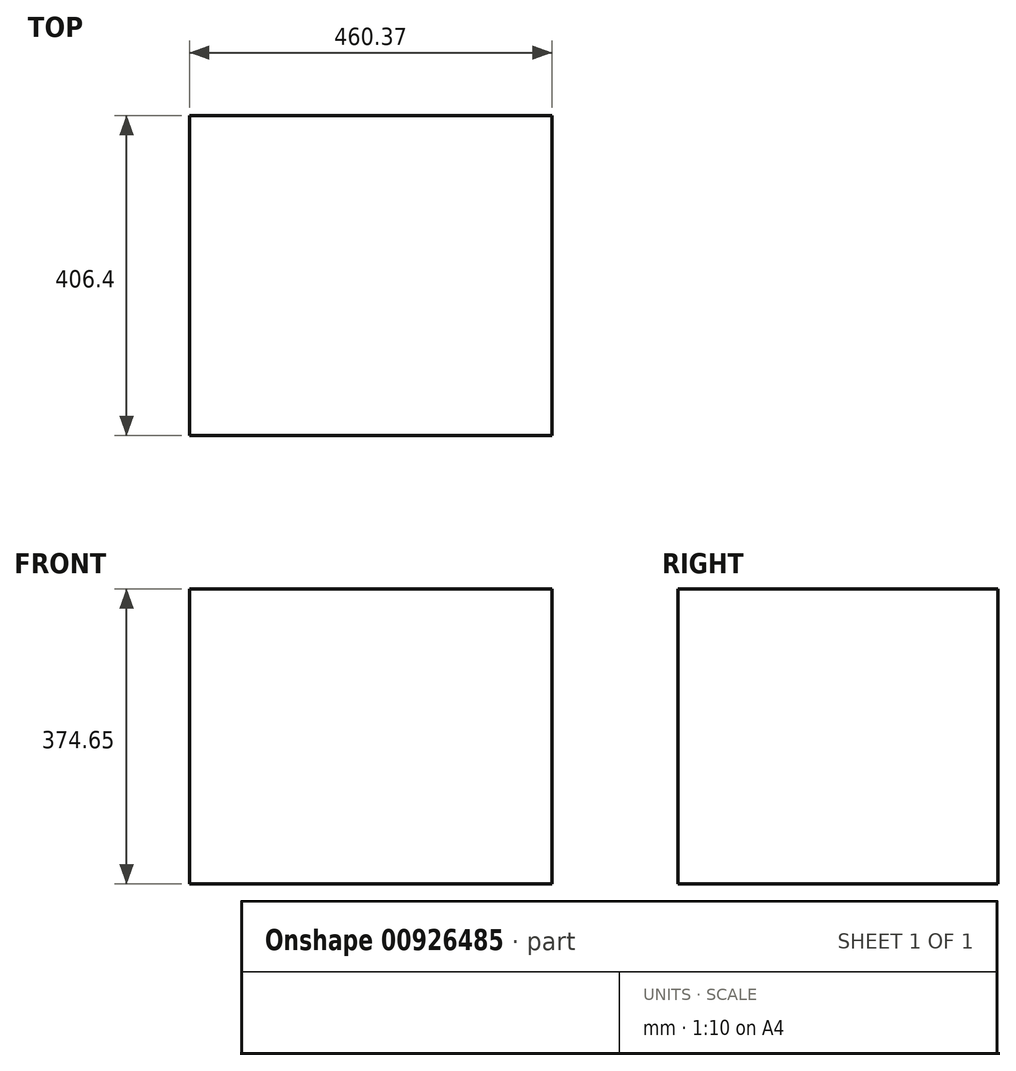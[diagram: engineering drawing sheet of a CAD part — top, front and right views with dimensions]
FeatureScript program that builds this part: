
annotation { "Feature Type Name" : "Feature", "Feature Type Description" : "" }
export const myFeature = defineFeature(function(context is Context, id is Id, definition is map)
    precondition{}
    {
        {
            var Q0;
            Q0=qCreatedBy(makeId("Front.planeOp"),FACE);
            var sketch = newSketch(context, id + "F0", { "sketchPlane" : qUnion([Q0])});
            skLineSegment(sketch, "E0", {"start": v(-99.63, 0) * mm, "end": v(360.74, 0) * mm});
            skLineSegment(sketch, "E1", {"start": v(360.74, 0) * mm, "end": v(360.74, 374.65) * mm});
            skLineSegment(sketch, "E2", {"start": v(360.74, 374.65) * mm, "end": v(-99.63, 374.65) * mm});
            skLineSegment(sketch, "E3", {"start": v(-99.63, 374.65) * mm, "end": v(-99.63, 0) * mm});
            skSolve(sketch);
        }
        {
            var Q0;
            Q0 = qSketchRegion(id + "F0", true);
            extrude(context, id + "F1", {"entities" : qUnion([Q0]), "depth" : 406.4 * mm, "offsetDistance" : 25.4 * mm});
        }
    });
